# Revit family: MOD 3-P-ID
name_source: partatom
category: Lighting Fixtures
units: mm (PartAtom-declared; Revit-internal decimal feet)

## family parameters
Cut with Voids When Loaded = No
Host = Face
Light Source = Yes
OmniClass Number = 23.80.70.11.14.17
OmniClass Title = Direct/Indirect
Part Type = Normal
Room Calculation Point = No
Round Connector Dimension = Use Diameter
Shared = Yes

## types (6) — shared parameters
Apparent Load = 0 VA
Assembly Code = D5020200
Color Filter = 16777215
Default Elevation = 4' - 0"
Description = The MODx family is an affordably-priced, full-featured offering with best-in-class attention to detail
Dimming Lamp Color Temperature Shift = <None>
Downlight Diffuser = Blade Baffle/Soft Glow Lens/Regressed Diffuse Lens/Asymmetric Diffuser Lens
Emit Shape Visible in Rendering = No
Emit from Rectangle Length = 0' - 3"
Fixture Distribution = Indirect/Direct; Indirect/Asymmetric Direct
Glass = Glass -White
Housing Material = Paint - Matte White
Lamp = LED
Load Classification = Lighting
Manufacturer = Litecontrol
Model = MOD 3 LED Pendant Indirect/Direct
Mounting = Pendant
Photometric Notes = More IES files download on Photometric Link
Photometric Web File = 3L-P-ID-LPA-4-SOF-X-CX-35K-I030-D030.ies
Power Factor = 1
Tilt Angle = -90.00°
Type Comments = Lighting Fixture
URL = https://www.currentlighting.com
Voltage = 120 V
Warranty = 5-Years Warranty
Wattage Comments = Variable Intensity technology provides specifiable lumen output/wattage

## per-type parameters (varying)
| type | Emit from Rectangle Width | zz Length 1 |
| MOD3-P-ID-04 | 3' - 11" | 4' - 0" |
| MOD3-P-ID-02 | 1' - 11" | 2' - 0" |
| MOD3-P-ID-03 | 2' - 11" | 3' - 0" |
| MOD3-P-ID-05 | 4' - 11" | 5' - 0" |
| MOD3-P-ID-06 | 5' - 11" | 6' - 0" |
| MOD3-P-ID-08 | 7' - 11" | 8' - 0" |

## geometry (parser evidence)
native form markers: Sweep x5
no freeform markers — native parametric forms only
